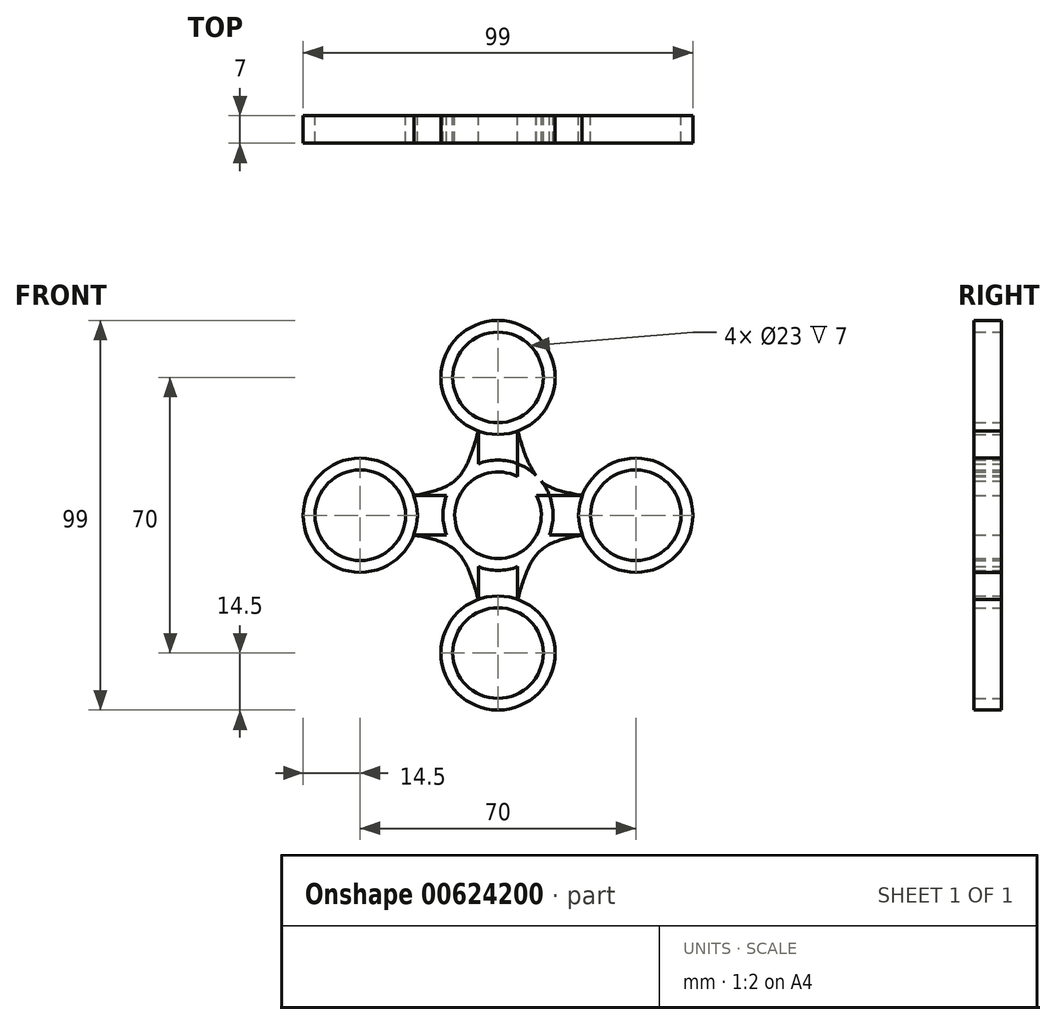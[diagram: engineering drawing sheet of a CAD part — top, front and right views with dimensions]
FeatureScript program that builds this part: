
annotation { "Feature Type Name" : "Feature", "Feature Type Description" : "" }
export const myFeature = defineFeature(function(context is Context, id is Id, definition is map)
    precondition{}
    {
        {
            var Q0;
            Q0=qCreatedBy(makeId("Front.planeOp"),FACE);
            var sketch = newSketch(context, id + "F0", { "sketchPlane" : qUnion([Q0])});
            skCircle(sketch, "E0", {"center": v(0, 0) * mm, "radius": 11 * mm});
            skLineSegment(sketch, "E1.bottom", {"start": v(-5, 35) * mm, "end": v(5, 35) * mm});
            skLineSegment(sketch, "E1.top", {"start": v(-5, -35) * mm, "end": v(5, -35) * mm});
            skLineSegment(sketch, "E1.left", {"start": v(-5, 35) * mm, "end": v(-5, -35) * mm});
            skLineSegment(sketch, "E1.right", {"start": v(5, 35) * mm, "end": v(5, -35) * mm});
            skLineSegment(sketch, "E2.bottom", {"start": v(35, -5) * mm, "end": v(-35, -5) * mm});
            skLineSegment(sketch, "E2.top", {"start": v(35, 5) * mm, "end": v(-35, 5) * mm});
            skLineSegment(sketch, "E2.left", {"start": v(35, -5) * mm, "end": v(35, 5) * mm});
            skLineSegment(sketch, "E2.right", {"start": v(-35, -5) * mm, "end": v(-35, 5) * mm});
            skCircle(sketch, "E3", {"center": v(0, 35) * mm, "radius": 11.5 * mm});
            skCircle(sketch, "E4", {"center": v(-35, 0) * mm, "radius": 11.5 * mm});
            skCircle(sketch, "E5", {"center": v(0, -35) * mm, "radius": 11.5 * mm});
            skCircle(sketch, "E6", {"center": v(35, 0) * mm, "radius": 11.5 * mm});
            skCircle(sketch, "E7.0", {"center": v(-35, 0) * mm, "radius": 14.5 * mm});
            skCircle(sketch, "E8.0", {"center": v(0, -35) * mm, "radius": 14.5 * mm});
            skCircle(sketch, "E9.0", {"center": v(35, 0) * mm, "radius": 14.5 * mm});
            skCircle(sketch, "E10.0", {"center": v(0, 35) * mm, "radius": 14.5 * mm});
            skCircle(sketch, "E11.0", {"center": v(0, 0) * mm, "radius": 14 * mm});
            skFitSpline(sketch, "E12", {"points": [v(21.39, 5) * mm, v(11, 8.66) * mm, v(5, 21.39) * mm], "startDerivative": vector(-25.26, 5.03) * mm, "endDerivative": vector(-7.74, 27.47) * mm});
            skFitSpline(sketch, "E13", {"points": [v(-5, 21.39) * mm, v(-10.63, 9.1) * mm, v(-21.39, 5) * mm], "startDerivative": vector(-7.8, -27.55) * mm, "endDerivative": vector(-25.2, -4.93) * mm});
            skFitSpline(sketch, "E14", {"points": [v(-21.39, -5) * mm, v(-10.63, -9.1) * mm, v(-5, -21.39) * mm], "startDerivative": vector(25.19, -4.94) * mm, "endDerivative": vector(7.82, -27.53) * mm});
            skLineSegment(sketch, "E15", {"start": v(-10.63, -9.1) * mm, "end": v(14.78, -9.1) * mm});
            skFitSpline(sketch, "E16", {"points": [v(21.39, -5) * mm, v(10.63, -9.1) * mm, v(5, -21.39) * mm], "startDerivative": vector(-25.19, -4.94) * mm, "endDerivative": vector(-7.82, -27.53) * mm});
            skFitSpline(sketch, "E17", {"points": [v(11.62, -9.1) * mm, v(12.6, -9.1) * mm, v(13.92, -11.97) * mm], "startDerivative": vector(2.85, 0.8) * mm, "endDerivative": vector(1.85, -5.88) * mm});
            skSolve(sketch);
        }
        {
            var Q0;
            {var subQ1=sQuery(id+"F0.wireOp",EDGE,"E1.left");var subQ3=sQuery(id+"F0.wireOp",EDGE,"E5");var subQ4=makeQuery(id+"F0.imprint","INTERSECT",VERTEX,{"derivedFrom":[subQ1,subQ3]});Q0=makeQuery(id+"F0.imprint","IMPRINT",FACE,{"disambiguationData":[TD([[makeQuery(id+"F0.imprint","IMPRINT",EDGE,{"disambiguationData":[TD([[subQ4,-1.0]])],"derivedFrom":subQ3}),-1.0]])]});}
            var Q1;
            {var subQ1=sQuery(id+"F0.wireOp",EDGE,"E2.bottom");var subQ3=sQuery(id+"F0.wireOp",EDGE,"E6");var subQ4=makeQuery(id+"F0.imprint","INTERSECT",VERTEX,{"derivedFrom":[subQ1,subQ3]});Q1=makeQuery(id+"F0.imprint","IMPRINT",FACE,{"disambiguationData":[TD([[makeQuery(id+"F0.imprint","IMPRINT",EDGE,{"disambiguationData":[TD([[subQ4,-1.0]])],"derivedFrom":subQ3}),-1.0]])]});}
            var Q2;
            {var subQ1=sQuery(id+"F0.wireOp",EDGE,"E2.bottom");var subQ3=sQuery(id+"F0.wireOp",EDGE,"E6");var subQ4=makeQuery(id+"F0.imprint","INTERSECT",VERTEX,{"derivedFrom":[subQ1,subQ3]});Q2=makeQuery(id+"F0.imprint","IMPRINT",FACE,{"disambiguationData":[TD([[makeQuery(id+"F0.imprint","IMPRINT",EDGE,{"disambiguationData":[TD([[subQ4,1.0]])],"derivedFrom":subQ3}),-1.0]])]});}
            var Q3;
            {var subQ1=sQuery(id+"F0.wireOp",EDGE,"E2.bottom");var subQ3=sQuery(id+"F0.wireOp",EDGE,"E11.0");var subQ4=makeQuery(id+"F0.imprint","INTERSECT",VERTEX,{"disambiguationData":[OD(0.0)],"derivedFrom":[subQ1,subQ3]});Q3=makeQuery(id+"F0.imprint","IMPRINT",FACE,{"disambiguationData":[TD([[makeQuery(id+"F0.imprint","IMPRINT",EDGE,{"disambiguationData":[TD([[subQ4,-1.0]])],"derivedFrom":subQ3}),-1.0]])]});}
            var Q4;
            {var subQ1=sQuery(id+"F0.wireOp",EDGE,"E2.bottom");var subQ3=sQuery(id+"F0.wireOp",EDGE,"E11.0");var subQ4=makeQuery(id+"F0.imprint","INTERSECT",VERTEX,{"disambiguationData":[OD(1.0)],"derivedFrom":[subQ1,subQ3]});Q4=makeQuery(id+"F0.imprint","IMPRINT",FACE,{"disambiguationData":[TD([[makeQuery(id+"F0.imprint","IMPRINT",EDGE,{"disambiguationData":[TD([[subQ4,1.0]])],"derivedFrom":subQ3}),-1.0]])]});}
            var Q5;
            {var subQ1=sQuery(id+"F0.wireOp",EDGE,"E1.left");var subQ3=sQuery(id+"F0.wireOp",EDGE,"E11.0");var subQ4=makeQuery(id+"F0.imprint","INTERSECT",VERTEX,{"disambiguationData":[OD(1.0)],"derivedFrom":[subQ1,subQ3]});Q5=makeQuery(id+"F0.imprint","IMPRINT",FACE,{"disambiguationData":[TD([[makeQuery(id+"F0.imprint","IMPRINT",EDGE,{"disambiguationData":[TD([[subQ4,-1.0]])],"derivedFrom":subQ3}),-1.0]])]});}
            var Q6;
            {var subQ1=sQuery(id+"F0.wireOp",EDGE,"E1.left");var subQ3=sQuery(id+"F0.wireOp",EDGE,"E11.0");var subQ4=makeQuery(id+"F0.imprint","INTERSECT",VERTEX,{"disambiguationData":[OD(0.0)],"derivedFrom":[subQ1,subQ3]});Q6=makeQuery(id+"F0.imprint","IMPRINT",FACE,{"disambiguationData":[TD([[makeQuery(id+"F0.imprint","IMPRINT",EDGE,{"disambiguationData":[TD([[subQ4,1.0]])],"derivedFrom":subQ3}),-1.0]])]});}
            var Q7;
            {var subQ1=sQuery(id+"F0.wireOp",EDGE,"E1.left");var subQ3=sQuery(id+"F0.wireOp",EDGE,"E3");var subQ4=makeQuery(id+"F0.imprint","INTERSECT",VERTEX,{"derivedFrom":[subQ1,subQ3]});Q7=makeQuery(id+"F0.imprint","IMPRINT",FACE,{"disambiguationData":[TD([[makeQuery(id+"F0.imprint","IMPRINT",EDGE,{"disambiguationData":[TD([[subQ4,-1.0]])],"derivedFrom":subQ3}),-1.0]])]});}
            var Q8;
            {var subQ1=sQuery(id+"F0.wireOp",EDGE,"E1.left");var subQ3=sQuery(id+"F0.wireOp",EDGE,"E3");var subQ4=makeQuery(id+"F0.imprint","INTERSECT",VERTEX,{"derivedFrom":[subQ1,subQ3]});Q8=makeQuery(id+"F0.imprint","IMPRINT",FACE,{"disambiguationData":[TD([[makeQuery(id+"F0.imprint","IMPRINT",EDGE,{"disambiguationData":[TD([[subQ4,1.0]])],"derivedFrom":subQ3}),-1.0]])]});}
            var Q9;
            {var subQ1=sQuery(id+"F0.wireOp",EDGE,"E2.bottom");var subQ3=sQuery(id+"F0.wireOp",EDGE,"E4");var subQ4=makeQuery(id+"F0.imprint","INTERSECT",VERTEX,{"derivedFrom":[subQ1,subQ3]});Q9=makeQuery(id+"F0.imprint","IMPRINT",FACE,{"disambiguationData":[TD([[makeQuery(id+"F0.imprint","IMPRINT",EDGE,{"disambiguationData":[TD([[subQ4,1.0]])],"derivedFrom":subQ3}),-1.0]])]});}
            var Q10;
            {var subQ1=sQuery(id+"F0.wireOp",EDGE,"E2.bottom");var subQ3=sQuery(id+"F0.wireOp",EDGE,"E4");var subQ4=makeQuery(id+"F0.imprint","INTERSECT",VERTEX,{"derivedFrom":[subQ1,subQ3]});Q10=makeQuery(id+"F0.imprint","IMPRINT",FACE,{"disambiguationData":[TD([[makeQuery(id+"F0.imprint","IMPRINT",EDGE,{"disambiguationData":[TD([[subQ4,-1.0]])],"derivedFrom":subQ3}),-1.0]])]});}
            var Q11;
            {var subQ1=sQuery(id+"F0.wireOp",EDGE,"E1.left");var subQ3=sQuery(id+"F0.wireOp",EDGE,"E5");var subQ4=makeQuery(id+"F0.imprint","INTERSECT",VERTEX,{"derivedFrom":[subQ1,subQ3]});Q11=makeQuery(id+"F0.imprint","IMPRINT",FACE,{"disambiguationData":[TD([[makeQuery(id+"F0.imprint","IMPRINT",EDGE,{"disambiguationData":[TD([[subQ4,1.0]])],"derivedFrom":subQ3}),-1.0]])]});}
            var Q12;
            {var subQ0=sQuery(id+"F0.wireOp",EDGE,"E1.left");var subQ1=sQuery(id+"F0.wireOp",EDGE,"E0");var subQ2=makeQuery(id+"F0.imprint","INTERSECT",VERTEX,{"disambiguationData":[OD(1.0)],"derivedFrom":[subQ1,subQ0]});Q12=makeQuery(id+"F0.imprint","IMPRINT",FACE,{"disambiguationData":[TD([[makeQuery(id+"F0.imprint","IMPRINT",EDGE,{"disambiguationData":[TD([[subQ2,-1.0]])],"derivedFrom":subQ1}),-1.0]])]});}
            var Q13;
            {var subQ1=sQuery(id+"F0.wireOp",EDGE,"E0");var subQ7=sQuery(id+"F0.wireOp",EDGE,"E1.right");var subQ9=makeQuery(id+"F0.imprint","INTERSECT",VERTEX,{"disambiguationData":[OD(1.0)],"derivedFrom":[subQ1,subQ7]});Q13=makeQuery(id+"F0.imprint","IMPRINT",FACE,{"disambiguationData":[TD([[makeQuery(id+"F0.imprint","IMPRINT",EDGE,{"disambiguationData":[TD([[subQ9,-1.0]])],"derivedFrom":subQ1}),-1.0]])]});}
            var Q14;
            {var subQ0=sQuery(id+"F0.wireOp",EDGE,"E15");var subQ1=sQuery(id+"F0.wireOp",EDGE,"E0");var subQ2=makeQuery(id+"F0.imprint","INTERSECT",VERTEX,{"disambiguationData":[OD(1.0)],"derivedFrom":[subQ1,subQ0]});Q14=makeQuery(id+"F0.imprint","IMPRINT",FACE,{"disambiguationData":[TD([[makeQuery(id+"F0.imprint","IMPRINT",EDGE,{"disambiguationData":[TD([[subQ2,-1.0]])],"derivedFrom":subQ1}),-1.0]])]});}
            var Q15;
            {var subQ0=sQuery(id+"F0.wireOp",EDGE,"E2.top");var subQ1=sQuery(id+"F0.wireOp",EDGE,"E0");var subQ2=makeQuery(id+"F0.imprint","INTERSECT",VERTEX,{"disambiguationData":[OD(0.0)],"derivedFrom":[subQ1,subQ0]});Q15=makeQuery(id+"F0.imprint","IMPRINT",FACE,{"disambiguationData":[TD([[makeQuery(id+"F0.imprint","IMPRINT",EDGE,{"disambiguationData":[TD([[subQ2,1.0]])],"derivedFrom":subQ1}),-1.0]])]});}
            var Q16;
            {var subQ5=sQuery(id+"F0.wireOp",EDGE,"E1.right");var subQ6=sQuery(id+"F0.wireOp",EDGE,"E0");var subQ7=makeQuery(id+"F0.imprint","INTERSECT",VERTEX,{"disambiguationData":[OD(0.0)],"derivedFrom":[subQ6,subQ5]});Q16=makeQuery(id+"F0.imprint","IMPRINT",FACE,{"disambiguationData":[TD([[makeQuery(id+"F0.imprint","IMPRINT",EDGE,{"disambiguationData":[TD([[subQ7,1.0]])],"derivedFrom":subQ6}),-1.0]])]});}
            var Q17;
            {var subQ0=sQuery(id+"F0.wireOp",EDGE,"E1.right");var subQ1=sQuery(id+"F0.wireOp",EDGE,"E0");var subQ2=makeQuery(id+"F0.imprint","INTERSECT",VERTEX,{"disambiguationData":[OD(0.0)],"derivedFrom":[subQ1,subQ0]});Q17=makeQuery(id+"F0.imprint","IMPRINT",FACE,{"disambiguationData":[TD([[makeQuery(id+"F0.imprint","IMPRINT",EDGE,{"disambiguationData":[TD([[subQ2,-1.0]])],"derivedFrom":subQ1}),-1.0]])]});}
            var Q18;
            {var subQ1=sQuery(id+"F0.wireOp",EDGE,"E0");var subQ7=sQuery(id+"F0.wireOp",EDGE,"E1.left");var subQ9=makeQuery(id+"F0.imprint","INTERSECT",VERTEX,{"disambiguationData":[OD(0.0)],"derivedFrom":[subQ1,subQ7]});Q18=makeQuery(id+"F0.imprint","IMPRINT",FACE,{"disambiguationData":[TD([[makeQuery(id+"F0.imprint","IMPRINT",EDGE,{"disambiguationData":[TD([[subQ9,-1.0]])],"derivedFrom":subQ1}),-1.0]])]});}
            var Q19;
            {var subQ0=sQuery(id+"F0.wireOp",EDGE,"E2.top");var subQ1=sQuery(id+"F0.wireOp",EDGE,"E0");var subQ2=makeQuery(id+"F0.imprint","INTERSECT",VERTEX,{"disambiguationData":[OD(1.0)],"derivedFrom":[subQ1,subQ0]});Q19=makeQuery(id+"F0.imprint","IMPRINT",FACE,{"disambiguationData":[TD([[makeQuery(id+"F0.imprint","IMPRINT",EDGE,{"disambiguationData":[TD([[subQ2,-1.0]])],"derivedFrom":subQ1}),-1.0]])]});}
            var Q20;
            {var subQ0=sQuery(id+"F0.wireOp",EDGE,"E2.bottom");var subQ1=sQuery(id+"F0.wireOp",EDGE,"E0");var subQ2=makeQuery(id+"F0.imprint","INTERSECT",VERTEX,{"disambiguationData":[OD(0.0)],"derivedFrom":[subQ1,subQ0]});Q20=makeQuery(id+"F0.imprint","IMPRINT",FACE,{"disambiguationData":[TD([[makeQuery(id+"F0.imprint","IMPRINT",EDGE,{"disambiguationData":[TD([[subQ2,-1.0]])],"derivedFrom":subQ1}),-1.0]])]});}
            var Q21;
            {var subQ0=sQuery(id+"F0.wireOp",EDGE,"E15");var subQ7=sQuery(id+"F0.wireOp",EDGE,"E0");var subQ9=makeQuery(id+"F0.imprint","INTERSECT",VERTEX,{"disambiguationData":[OD(0.0)],"derivedFrom":[subQ7,subQ0]});Q21=makeQuery(id+"F0.imprint","IMPRINT",FACE,{"disambiguationData":[TD([[makeQuery(id+"F0.imprint","IMPRINT",EDGE,{"disambiguationData":[TD([[subQ9,-1.0]])],"derivedFrom":subQ7}),-1.0]])]});}
            var Q22;
            {var subQ0=sQuery(id+"F0.wireOp",EDGE,"E14");var subQ3=sQuery(id+"F0.wireOp",EDGE,"E11.0");var subQ5=makeQuery(id+"F0.imprint","INTERSECT",VERTEX,{"derivedFrom":[subQ3,subQ0]});Q22=makeQuery(id+"F0.imprint","IMPRINT",FACE,{"disambiguationData":[TD([[makeQuery(id+"F0.imprint","IMPRINT",EDGE,{"disambiguationData":[TD([[subQ5,-1.0]])],"derivedFrom":subQ3}),-1.0]])]});}
            var Q23;
            {var subQ0=sQuery(id+"F0.wireOp",EDGE,"E16");var subQ3=sQuery(id+"F0.wireOp",EDGE,"E11.0");var subQ5=makeQuery(id+"F0.imprint","INTERSECT",VERTEX,{"derivedFrom":[subQ3,subQ0]});Q23=makeQuery(id+"F0.imprint","IMPRINT",FACE,{"disambiguationData":[TD([[makeQuery(id+"F0.imprint","IMPRINT",EDGE,{"disambiguationData":[TD([[subQ5,1.0]])],"derivedFrom":subQ3}),-1.0]])]});}
            var Q24;
            {var subQ0=sQuery(id+"F0.wireOp",EDGE,"E12");var subQ3=sQuery(id+"F0.wireOp",EDGE,"E11.0");var subQ5=makeQuery(id+"F0.imprint","INTERSECT",VERTEX,{"disambiguationData":[OD(1.0)],"derivedFrom":[subQ3,subQ0]});Q24=makeQuery(id+"F0.imprint","IMPRINT",FACE,{"disambiguationData":[TD([[makeQuery(id+"F0.imprint","IMPRINT",EDGE,{"disambiguationData":[TD([[subQ5,-1.0]])],"derivedFrom":subQ3}),-1.0]])]});}
            var Q25;
            {var subQ0=sQuery(id+"F0.wireOp",EDGE,"E12");var subQ3=sQuery(id+"F0.wireOp",EDGE,"E11.0");var subQ5=makeQuery(id+"F0.imprint","INTERSECT",VERTEX,{"disambiguationData":[OD(0.0)],"derivedFrom":[subQ3,subQ0]});Q25=makeQuery(id+"F0.imprint","IMPRINT",FACE,{"disambiguationData":[TD([[makeQuery(id+"F0.imprint","IMPRINT",EDGE,{"disambiguationData":[TD([[subQ5,1.0]])],"derivedFrom":subQ3}),-1.0]])]});}
            var Q26;
            {var subQ1=sQuery(id+"F0.wireOp",EDGE,"E2.bottom");var subQ3=sQuery(id+"F0.wireOp",EDGE,"E11.0");var subQ4=makeQuery(id+"F0.imprint","INTERSECT",VERTEX,{"disambiguationData":[OD(0.0)],"derivedFrom":[subQ1,subQ3]});Q26=makeQuery(id+"F0.imprint","IMPRINT",FACE,{"disambiguationData":[TD([[makeQuery(id+"F0.imprint","IMPRINT",EDGE,{"disambiguationData":[TD([[subQ4,1.0]])],"derivedFrom":subQ1}),1.0]])]});}
            var Q27;
            {var subQ0=sQuery(id+"F0.wireOp",EDGE,"E13");var subQ3=sQuery(id+"F0.wireOp",EDGE,"E11.0");var subQ5=makeQuery(id+"F0.imprint","INTERSECT",VERTEX,{"disambiguationData":[OD(0.0)],"derivedFrom":[subQ3,subQ0]});Q27=makeQuery(id+"F0.imprint","IMPRINT",FACE,{"disambiguationData":[TD([[makeQuery(id+"F0.imprint","IMPRINT",EDGE,{"disambiguationData":[TD([[subQ5,1.0]])],"derivedFrom":subQ3}),-1.0]])]});}
            var Q28;
            {var subQ0=sQuery(id+"F0.wireOp",EDGE,"E13");var subQ3=sQuery(id+"F0.wireOp",EDGE,"E11.0");var subQ5=makeQuery(id+"F0.imprint","INTERSECT",VERTEX,{"disambiguationData":[OD(1.0)],"derivedFrom":[subQ3,subQ0]});Q28=makeQuery(id+"F0.imprint","IMPRINT",FACE,{"disambiguationData":[TD([[makeQuery(id+"F0.imprint","IMPRINT",EDGE,{"disambiguationData":[TD([[subQ5,-1.0]])],"derivedFrom":subQ3}),-1.0]])]});}
            var Q29;
            {var subQ1=sQuery(id+"F0.wireOp",EDGE,"E2.bottom");var subQ3=sQuery(id+"F0.wireOp",EDGE,"E11.0");var subQ4=makeQuery(id+"F0.imprint","INTERSECT",VERTEX,{"disambiguationData":[OD(1.0)],"derivedFrom":[subQ1,subQ3]});Q29=makeQuery(id+"F0.imprint","IMPRINT",FACE,{"disambiguationData":[TD([[makeQuery(id+"F0.imprint","IMPRINT",EDGE,{"disambiguationData":[TD([[subQ4,-1.0]])],"derivedFrom":subQ1}),1.0]])]});}
            extrude(context, id + "F1", {"entities" : qUnion([Q0, Q1, Q2, Q3, Q4, Q5, Q6, Q7, Q8, Q9, Q10, Q11, Q12, Q13, Q14, Q15, Q16, Q17, Q18, Q19, Q20, Q21, Q22, Q23, Q24, Q25, Q26, Q27, Q28, Q29]), "depth" : 7 * mm, "offsetDistance" : 25 * mm});
        }
    });
